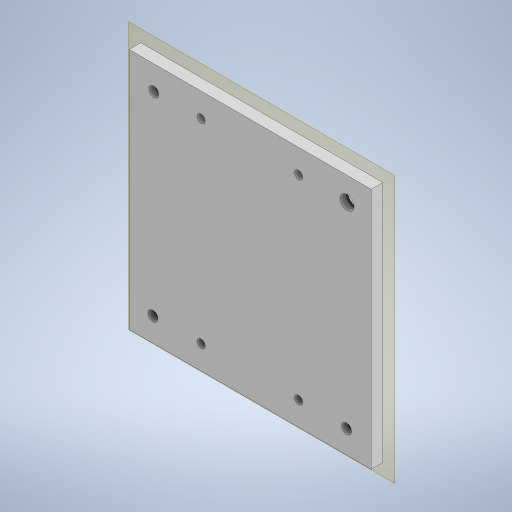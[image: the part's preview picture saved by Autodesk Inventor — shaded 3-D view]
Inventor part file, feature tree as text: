
AUTODESK INVENTOR PART (.ipt)
format: ipt  version: 2023.2 (Build 272271000, 271)  size: 390,144 bytes
history: native  units: mm
features: reference x16, sketch x4, hole x3, other x3, plane x1, extrude x1
ambient origin geometry x8: Origin, YZ Plane, XZ Plane, XY Plane, X Axis, Y Axis, Z Axis, Center Point
bodies: Solid1 (feature_tree)
feature tree (28):
  plane  "Work Plane1"
  extrude  "Extrusion1"  [1 undecoded]
  hole  "Hole1"  [1 undecoded]
  hole  "Hole2"  [1 undecoded]
  hole  "Hole3"  [1 undecoded]
  sketch  "Sketch3"  dims[d8=6.0mm d9=0.0mm]
  reference  "Reference15"
  reference  "Reference16"
  reference  "Reference17"
  reference  "Reference18"
  reference  "Reference19"
  reference  "Reference20"
  reference  "Reference21"
  reference  "Reference22"
  reference  "Reference23"
  reference  "Reference24"
  reference  "Reference25"
  reference  "Reference26"
  reference  "Reference27"
  reference  "Reference28"
  reference  "Reference29"
  reference  "Reference30"
  sketch  "Sketch4"  dims[d10=7.2mm d11=6.0mm d12=12.25mm d13=3.0mm d14=90.0deg d15=8.0mm d16=20.594885mm]
  sketch  "Sketch5"  dims[d17=5.1mm d18=6.0mm d19=9.2mm d20=3.0mm d21=90.0deg d22=8.0mm d23=20.594885mm]
  sketch  "Sketch6"  dims[d24=4.2mm d25=6.0mm d26=9.2mm d27=2.0mm d28=90.0deg d29=8.0mm d30=20.594885mm]
  parser-record x1  (decoder bookkeeping rows leaked as tree rows — omitted from the tree; the rows remain in map.json)
  other  "Main Assembly.iam"
  other  "Z axis carriage small:1"
note: 4 required parameter values undecoded (feature->parameter linkage not recoverable at this tier; creation-order binding heuristic only, values carry confidence <= 0.55)
note: 1 file-system path scrubbed to <path> (originals preserved in map.json)
